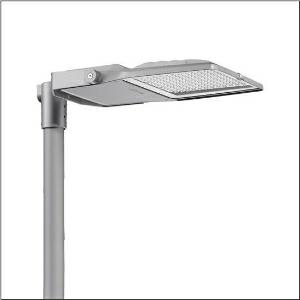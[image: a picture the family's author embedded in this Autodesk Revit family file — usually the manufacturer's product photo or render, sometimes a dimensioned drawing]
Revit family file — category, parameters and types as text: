
# Revit family: floodlight_fl_21_iq_midi___pl64_5xa7782e2e3a_fffa
name_source: partatom
category: Lighting Fixtures
units: mm (PartAtom-declared; Revit-internal decimal feet)

## family parameters
Cut with Voids When Loaded = No
Host = Face
Light Source = No
Part Type = Normal
Room Calculation Point = No
Round Connector Dimension = Use Diameter
Shared = No

## types (1)
- --- (1 x LED, 25930 lm, 208.1 W, 3000K)
    Apparent Load = 208 VA
    CIE Flux Codes = 28 80 98 100 100
    Color Rendering = 70
    Color Temperature = 3000K
    Default Elevation = 1800 mm
    Description = Floodlight FL 21 iQ midi, floodlight, primary light control with lens, of PMMA, primary optical cover: protective disc, of toughened safety glass, transparent, light distribution: PL64, light emission: direct distribution, installation type: surface-mounted, lamps: LED, High Power LED, rated values: 25.930lm | 208,1W | 124,6lm/W (begin service life); end service life: 25.930lm | 227,1W; at 50% lumin. flux: 12.965lm | 90,1W | 143,9lm/W, colour temperature: 3000K, colour rendering: CRI > 70, light colour: 730, light setting 1 begin service life: 100% | 25.930lm | 208,1W | 124,6lm/W | 3.000K, light setting 1 end service life: 227,1W, further light settings possible, control: optimised constant luminous flux control (CLO 2.0), Desk-Remote (wireless, voltage-free reading and setting of iQ features in the workshop via application-optimized NFC function/RFID function), Smart-Wire, Night-Set, Temp-Guard, Auto-Match, Street-Remote, pre-setting: linear dimming characteristic, with terminal, 6-pole, mains connection: 220..240V, AC, 50/60Hz, luminaire housing, of diecast aluminium, powder-coated, SITECO metallic grey (DB 702S), corrosivity category C5 mid according to DIN EN ISO 12944suitable for swimming poolschlorine-resistant, sealing non-destructively replaceable, please order mast flange separately, mast bracket, of steel, galvanised, powder-coated, SITECO metallic grey (DB 702S), protection rating (complete): IP66, insulation class (complete): insulation class II (safety insulation), certification: CE, ENEC, VDE, protection symbol: D, impact resistance: IK08, permissible operating ambient temperature: -40..+40°C, permissible operating ambient temperature for outdoor applications: -40..+50°C, standard: DIN EN 12944, LABS conformity tested according to VDMA 24364:2018-05, packaging unit: 1 piece

Light Distribution: PL64
    Height = 76 mm
    Lamp = 1 x LED
    Lamp Light Flux = 25930 lm
    Lamp Power = 208.1 W
    Lamp count = 1
    Length = 657 mm
    Luminous efficacy = 125 lm/W
    Manufacturer = Siteco
    ModVariant = No
    Model = 5XA7782E2E3A
    Number of Poles = 1
    OnlyDefault = Yes
    Power Factor = 1
    Product Name = Floodlight FL 21 iQ midi | PL64
    Product group = floodlight | pylon annexe
    ProductGroupID = 6201
    Protection Class = Protection class II
    Protection Degree = IP 66
    RLX_Detail_Level = 1
    RLX_Emergency_Light_Flux = 0 lm
    RLX_Emergency_Type = 0
    RLX_Emergency_Type_DB = No
    RlxData = <blob elided: 153825 chars, md5=24edc5a9>
    Socket = socket
    Standby Power = 0 W
    System Light Flux = 25930 lm
    System Power = 208 W
    Type Comments = factory setting: luminous flux: 100 % | dim-lin: 254 | 710 mA
    Type Image = l_1007123.jpg
    URL = http://relux.com
    VarID = @adj_107041
    Voltage = 0 V
    Weight = 0.00 kg
    Width = 442 mm

## geometry (parser evidence)
native form markers: Blend x4, Sweep x15
no freeform markers — native parametric forms only
